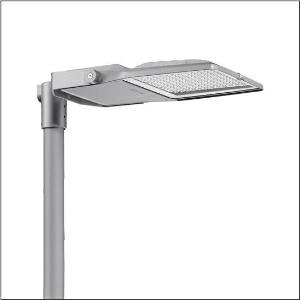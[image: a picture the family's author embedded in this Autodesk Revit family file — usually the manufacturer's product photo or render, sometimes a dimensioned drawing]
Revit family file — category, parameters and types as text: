
# Revit family: floodlight_fl_21_iq_midi___pl61_5xa7781e2c3a_352e
name_source: partatom
category: Lighting Fixtures
units: mm (PartAtom-declared; Revit-internal decimal feet)

## family parameters
Cut with Voids When Loaded = No
Host = Face
Light Source = No
Part Type = Normal
Room Calculation Point = No
Round Connector Dimension = Use Diameter
Shared = No

## types (1)
- --- (1 x LED, 26360 lm, 208.1 W, 3000K)
    Apparent Load = 208 VA
    CIE Flux Codes = 33 65 98 100 100
    Color Rendering = 70
    Color Temperature = 3000K
    Default Elevation = 1800 mm
    Description = Floodlight FL 21 iQ midi, floodlight, primary light control with lens, of PMMA, primary optical cover: protective disc, of toughened safety glass, transparent, light distribution: PL61, light emission: direct distribution, installation type: surface-mounted, LED, High Power LED, rated luminous flux: 26.360lm, luminous efficacy: 127lm/W, light colour: 730, colour temperature: 3000K, control gear: ECG iQ, control: optimised constant luminous flux control (CLO 2.0), Desk-Remote (wireless, voltage-free reading and setting of iQ features in the workshop via application-optimized NFC function/RFID function), Light-Fading, Smart-Wire, Night-Set, Lumen-Switch, Temp-Guard, Auto-Match, with terminal, 6-pole, mains connection: 220..240V, AC, 50/60Hz, start of lifetime: 208W, end of service life: 227W, reduction: 90W, luminaire housing, of diecast aluminium, powder-coated, Siteco® metallic grey (DB 702S), corrosivity category C5 mid according to DIN EN ISO 12944, sealing non-destructively replaceable, please order mast flange separately, mast bracket, of steel, galvanised, powder-coated, Siteco® metallic grey (DB 702S), protection rating (complete): IP66, insulation class (complete): insulation class II (safety insulation), certification: CE, ENEC, VDE, protection symbol: D, impact resistance: IK08, permissible operating ambient temperature: -40..+40°C, permissible operating ambient temperature for outdoor applications: -40..+50°C, standard: DIN EN 12944, LABS conformity tested according to VDMA 24364:2018-05, packaging unit: 1 piece

Light Distribution: PL61
    Height = 76 mm
    Lamp = 1 x LED
    Lamp Light Flux = 26360 lm
    Lamp Power = 208.1 W
    Lamp count = 1
    Length = 657 mm
    Luminous efficacy = 127 lm/W
    Manufacturer = Siteco
    ModVariant = No
    Model = 5XA7781E2C3A
    Number of Poles = 1
    OnlyDefault = Yes
    Power Factor = 1
    Product Name = Floodlight FL 21 iQ midi | PL61
    Product group = floodlight | pylon annexe
    ProductGroupID = 6200
    Protection Class = Protection class II
    Protection Degree = IP 66
    RLX_Detail_Level = 1
    RLX_Emergency_Light_Flux = 0 lm
    RLX_Emergency_Type = 0
    RLX_Emergency_Type_DB = No
    RlxData = <blob elided: 153813 chars, md5=fe021aed>
    Socket = socket
    Standby Power = 0 W
    System Light Flux = 26360 lm
    System Power = 208 W
    Type Comments = factory setting: luminous flux: 100 % | dim-lin: 254 | 710 mA
    Type Image = l_1007123.jpg
    URL = http://relux.com
    VarID = @adj_077785
    Voltage = 0 V
    Weight = 0.00 kg
    Width = 442 mm

## geometry (parser evidence)
native form markers: Blend x4, Sweep x16
no freeform markers — native parametric forms only
